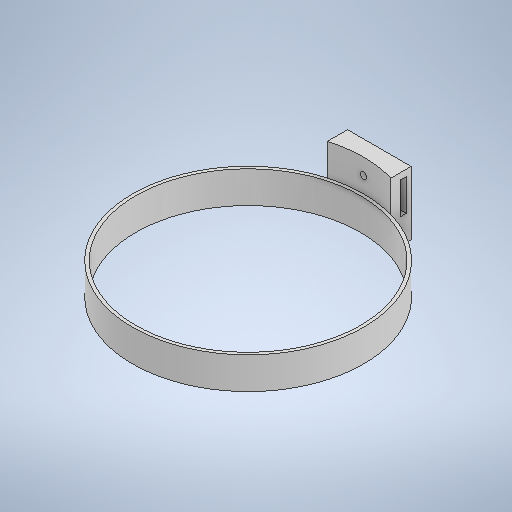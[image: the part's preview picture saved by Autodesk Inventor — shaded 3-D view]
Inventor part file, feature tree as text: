
AUTODESK INVENTOR PART (.ipt)
format: ipt  version: 2025 (Build 290162010, 162A)  size: 289,792 bytes
history: native  units: in
note: dims shown in document units (in); Inventor stores cm internally (conversion verified against a paired STEP export)
features: sketch x4, extrude x3, hole x1
ambient origin geometry x8: Origin, YZ Plane, XZ Plane, XY Plane, X Axis, Y Axis, Z Axis, Center Point
bodies: Solid1 (feature_tree)
feature tree (8):
  extrude  "Extrusion1"  Depth=3.63in
  extrude  "Extrusion2"  Depth=0.5in TaperAngle=0.0deg
  hole  "Hole1"  [1 undecoded]
  extrude  "Extrusion3"  Depth=0.5in
  sketch  "Sketch1"  dims[d0=3.53in d1=3.63in]
  sketch  "Sketch2"  dims[d2=0.5in d3=0.0in d4=0.5in d5=0.5in d6=0.0in d7=0.0in]
  sketch  "Sketch3"  dims[d8=1.0in d9=0.3189in]
  sketch  "Sketch4"  dims[d10=0.5in d11=0.25in d12=0.1in d13=0.75in d14=0.375in d15=0.25in d16=0.5635in d17=0.4322in d18=0.0in d19=0.1in d20=0.5in d21=0.35in d22=0.5in d23=0.0in]
note: 1 required parameter value undecoded (feature->parameter linkage not recoverable at this tier; creation-order binding heuristic only, values carry confidence <= 0.55)
